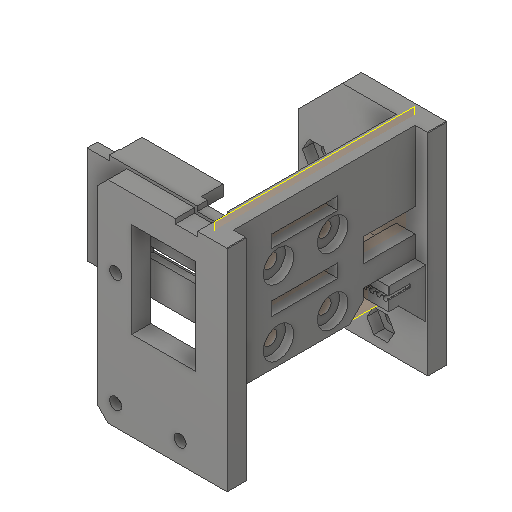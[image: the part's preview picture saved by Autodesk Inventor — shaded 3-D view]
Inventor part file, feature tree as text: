
AUTODESK INVENTOR PART (.ipt)
format: ipt  version: 2022 (Build 260153000, 153)  size: 799,744 bytes
history: native  units: in
note: dims shown in document units (in); Inventor stores cm internally (conversion verified against a paired STEP export)
features: projected_geometry x31, extrude x23, sketch x19, plane x12, chamfer x8, mirror x2, fillet x2, pattern_linear x2, sweep x1
ambient origin geometry x8: Origin, YZ Plane, XZ Plane, XY Plane, X Axis, Y Axis, Z Axis, Center Point
bodies: Solid1 (feature_tree)
feature tree (100):
  sketch  "Sketch1"  dims[d0=1.624in d1=1.3557in]
  extrude  "Extrusion1"  Depth=1.3557in
  extrude  "Extrusion2"  Depth=0.618in
  extrude  "Extrusion7"  Depth=0.146in
  extrude  "Extrusion9"  Depth=0.296in
  extrude  "Extrusion8"  Depth=0.161in
  sketch  "Sketch18"  dims[d11=0.356in d12=0.161in]
  plane  "Work Plane3"
  extrude  "Extrusion16"  Depth=0.161in
  extrude  "Extrusion17"  Depth=0.22in TaperAngle=0.0deg
  plane  "Work Plane4"
  plane  "Work Plane6"
  plane  "工作平面8"
  plane  "Work Plane7"
  mirror  "Mirror5"
  extrude  "Extrusion20"  Depth=0.942in
  extrude  "Extrusion21"  Depth=0.304in
  plane  "工作平面9"
  plane  "工作平面10"
  chamfer  "Chamfer2"  Distance=0.2515in
  extrude  "Extrusion27"  Depth=1.191in
  extrude  "Extrusion28"  Depth=1.128in
  fillet  "Fillet1"  Radius=0.16in
  pattern_linear  "Rectangular Pattern2"  Spacing1=0.126in  [1 undecoded]
  extrude  "Extrusion30"  TaperAngle=0.0deg  [1 undecoded]
  chamfer  "Chamfer5"  [1 undecoded]
  extrude  "Extrusion31"  Depth=0.126in
  sweep  "Sweep2"
  extrude  "Extrusion32"  Depth=0.1969in
  mirror  "Mirror6"
  extrude  "Extrusion33"  Depth=0.126in
  chamfer  "Chamfer6"  Distance=0.1181in
  extrude  "Extrusion35"  Depth=0.1181in TaperAngle=0.0deg
  chamfer  "Chamfer7"  Distance=0.5118in Angle=45.0deg
  plane  "工作平面14"
  plane  "工作平面11"
  plane  "工作平面12"
  extrude  "Extrusion38"  Depth=0.126in
  plane  "工作平面13"
  extrude  "Extrusion39"  Depth=2.45in
  extrude  "Extrusion40"  Depth=0.315in TaperAngle=0.0deg
  extrude  "拉伸41"  Depth=0.2441in TaperAngle=0.0deg
  chamfer  "倒角8"  Distance=0.0063in
  chamfer  "倒角9"  Distance=0.0787in
  plane  "工作平面15"
  extrude  "拉伸42"  Depth=0.126in
  extrude  "拉伸43"  Depth=0.126in
  fillet  "圆角5"  Radius=0.2756in
  pattern_linear  "矩形阵列4"  Spacing1=0.2441in  [1 undecoded]
  extrude  "拉伸44"  Depth=0.1181in TaperAngle=45.0deg
  chamfer  "倒角10"  Distance=0.2559in
  chamfer  "倒角11"  Distance=0.0551in
  sketch  "Sketch9"  dims[d5=0.774in d6=0.618in]
  projected_geometry  "Projected Loop4"
  sketch  "Sketch10"  dims[d7=0.262in d8=0.146in]
  sketch  "Sketch13"  dims[d9=0.765in d10=0.296in]
  projected_geometry  "Projected Loop9"
  projected_geometry  "Projected Loop10"
  projected_geometry  "Projected Loop11"
  projected_geometry  "Projected Loop12"
  sketch  "Sketch22"  dims[d13=0.356in d14=0.161in d15=0.356in d16=0.161in]
  projected_geometry  "Projected Loop16"
  projected_geometry  "Projected Loop17"
  projected_geometry  "Projected Loop20"
  projected_geometry  "Projected Loop21"
  sketch  "Sketch30"  dims[d17=0.356in d18=0.161in d19=0.22in d20=0.0in]
  projected_geometry  "Projected Loop31"
  sketch  "Sketch31"  dims[d21=0.122in d22=0.0in d48=0.942in]
  projected_geometry  "Projected Loop32"
  sketch  "Sketch32"  dims[d49=0.128in d50=0.304in d51=0.2515in d52=0.0in]
  projected_geometry  "Projected Loop33"
  projected_geometry  "Projected Loop34"
  projected_geometry  "Projected Loop35"
  sketch  "Sketch33"  dims[d63=1.733in d64=1.191in]
  projected_geometry  "Projected Loop36"
  projected_geometry  "Projected Loop37"
  projected_geometry  "Projected Loop38"
  projected_geometry  "Projected Loop39"
  projected_geometry  "Projected Loop41"
  projected_geometry  "Projected Loop42"
  projected_geometry  "Projected Loop43"
  sketch  "Sketch37"  dims[d65=0.12in d66=0.0in d67=1.128in d68=0.16in]
  projected_geometry  "Projected Loop44"
  projected_geometry  "Projected Loop45"
  projected_geometry  "Projected Loop46"
  projected_geometry  "Projected Loop47"
  projected_geometry  "Projected Loop48"
  sketch  "Sketch39"  dims[d69=0.161in]
  projected_geometry  "Projected Loop49"
  projected_geometry  "Projected Loop51"
  sketch  "Sketch41"  dims[d70=0.765in]
  sketch  "Sketch44"  dims[d71=0.075in d72=0.0in]
  sketch  "Sketch45"  dims[d116=0.3713in]
  projected_geometry  "Projected Loop60"
  projected_geometry  "Projected Loop61"
  projected_geometry  "Projected Loop64"
  sketch  "草图47"  dims[d117=0.6299in]
  sketch  "草图48"  dims[d149=0.0326in]
  sketch  "草图49"  dims[d150=1.313in d151=0.75in d152=1.19in d153=1.63in d154=0.14in d155=0.14in d156=0.14in d157=0.14in d160=0.28in d161=0.28in d162=0.1024in]
  sketch  "草图50"  dims[d164=0.22in d165=0.0in d166=0.126in d167=0.0in d168=0.0in d169=-0.622in d175=1.0556in d177=0.1969in d178=0.1969in d179=2.3622in d181=0.1181in d182=0.0in d183=0.1181in d184=0.0in d201=0.5118in d202=0.125in d203=45.0deg d222=2.7403in d223=2.45in d224=0.315in d225=0.0in d226=0.0472in d227=0.0335in d228=0.063in d229=0.0394in d230=0.0394in d233=0.2441in d234=0.0in d235=0.0063in d236=3.1496in d238=0.0787in d239=0.3937in d241=0.0787in d244=0.4791in d245=0.5906in d246=0.2756in d247=0.2441in d248=0.0in d249=0.1181in d250=0.125in d251=45.0deg d252=0.2559in d253=0.0551in d254=0.2559in d255=0.0551in d256=1.0in d257=0.0in d261=0.0787in d263=0.1181in d264=0.1181in d265=1.1811in d267=0.2362in d268=0.3937in d270=1.0in d272=0.1374in d273=0.0in d274=0.0in d277=1.0in d278=0.0in d279=0.1575in d280=1.0in d281=0.0in d282=0.765in d283=0.3825in d286=0.3937in d288=0.7874in d289=0.1575in d290=0.125in d291=45.0deg d296=0.1969in d297=0.0in d298=0.5118in d299=0.125in d300=45.0deg d308=0.0472in d309=0.0335in d310=0.0661in d311=0.0394in d312=0.0394in d313=0.2441in d314=0.0in d319=0.2441in d320=0.0in d322=0.1575in d323=0.2441in d324=0.0in d325=0.9843in d326=1.0in d327=0.0in d328=0.6in d329=0.6in d330=0.6in d331=0.6in d332=0.1181in d333=0.125in d334=45.0deg d335=0.1181in d336=0.125in d337=45.0deg d338=-0.11in d340=0.2559in d341=0.1181in d342=0.2362in d343=0.0in d344=0.1575in d345=0.0394in d346=0.0394in d347=0.0327in d348=0.011in d349=0.0472in d350=0.2441in d351=0.0in d353=0.0063in d354=3.5433in d356=0.0787in d357=1.3386in d358=0.4724in d359=0.0in d360=0.14in d361=0.14in d362=0.14in d363=0.75in d364=0.126in d365=0.0in d366=0.0039in d367=0.125in d368=45.0deg d369=0.0039in d370=0.125in d371=45.0deg]
note: 4 required parameter values undecoded (feature->parameter linkage not recoverable at this tier; creation-order binding heuristic only, values carry confidence <= 0.55)
